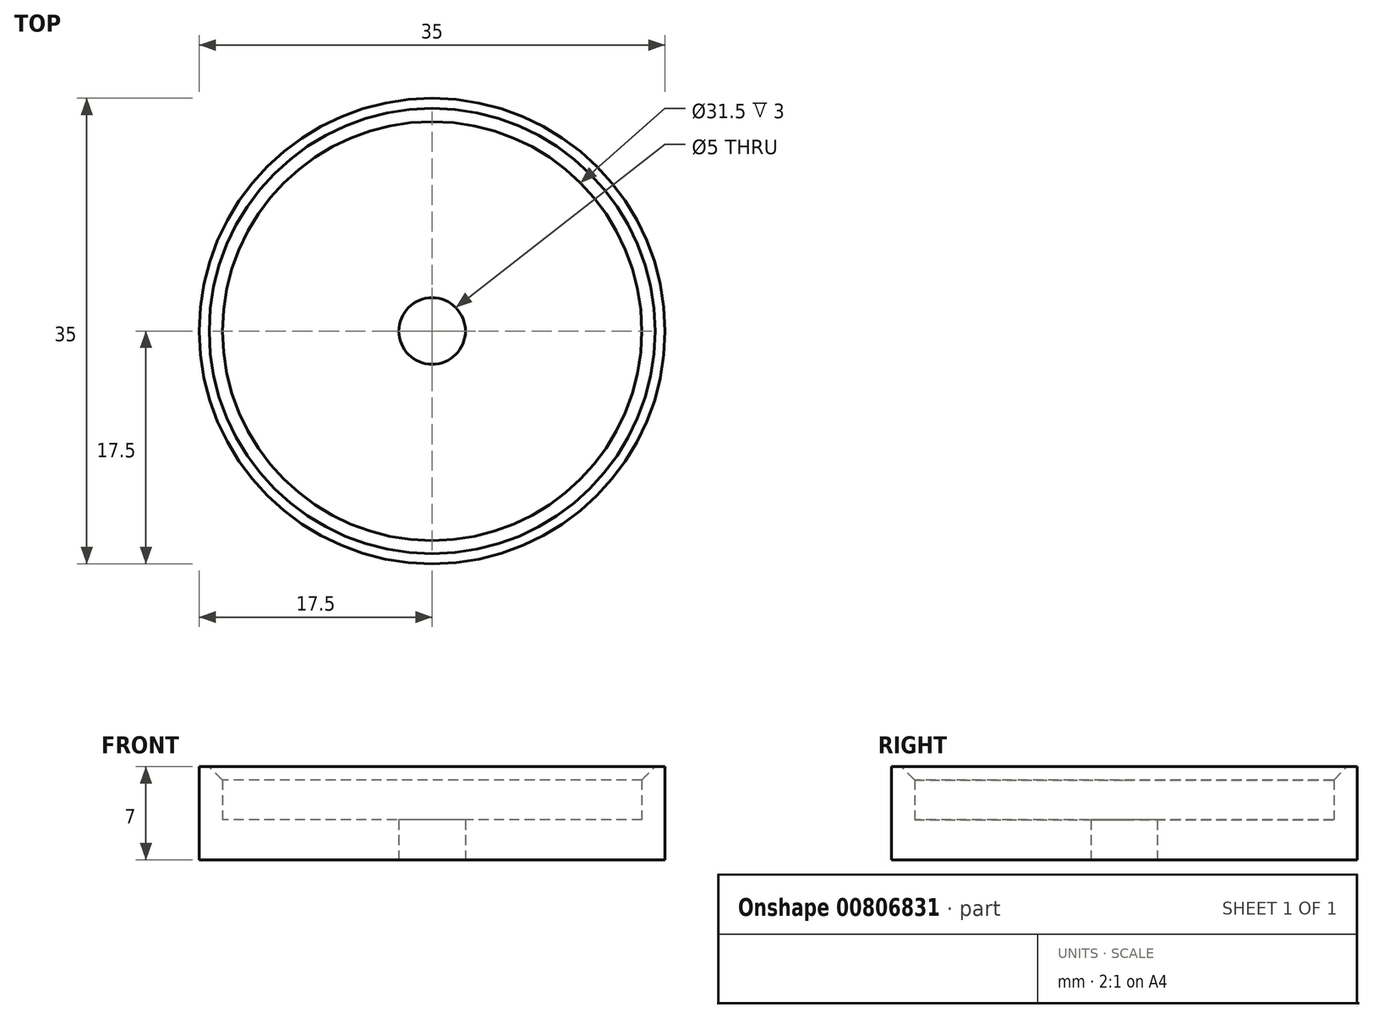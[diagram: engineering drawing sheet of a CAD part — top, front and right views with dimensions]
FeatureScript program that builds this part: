
annotation { "Feature Type Name" : "Feature", "Feature Type Description" : "" }
export const myFeature = defineFeature(function(context is Context, id is Id, definition is map)
    precondition{}
    {
        {
            var Q0;
            Q0=qCreatedBy(makeId("Top.planeOp"),FACE);
            var sketch = newSketch(context, id + "F0", { "sketchPlane" : qUnion([Q0])});
            skCircle(sketch, "E0", {"center": v(0, 0) * mm, "radius": 17.5 * mm});
            skCircle(sketch, "E1", {"center": v(0, 0) * mm, "radius": 15.75 * mm});
            skCircle(sketch, "E2", {"center": v(0, 0) * mm, "radius": 2.5 * mm});
            skSolve(sketch);
        }
        {
            var Q0;
            Q0=makeQuery(id+"F0.imprint","IMPRINT",FACE,{"disambiguationData":[TD([[makeQuery(id+"F0.imprint","IMPRINT",EDGE,{"derivedFrom":sQuery(id+"F0.wireOp",EDGE,"E0")}),1.0]])]});
            var Q1;
            {var subQ0=sQuery(id+"F0.wireOp",EDGE,"xPpbhzml-UGrW-7zZY-eOFT-DjyW9iULf8BB.bottom");var subQ1=sQuery(id+"F0.wireOp",EDGE,"E0");var subQ2=makeQuery(id+"F0.imprint","INTERSECT",VERTEX,{"disambiguationData":[OD(1.0)],"derivedFrom":[subQ1,subQ0]});Q1=makeQuery(id+"F0.imprint","IMPRINT",FACE,{"disambiguationData":[TD([[makeQuery(id+"F0.imprint","IMPRINT",EDGE,{"disambiguationData":[TD([[subQ2,-1.0]])],"derivedFrom":subQ1}),1.0]])]});}
            var Q2;
            {var subQ0=sQuery(id+"F0.wireOp",EDGE,"hrvuodh3-IVyE-woEC-Gxd3-sxO2CLI6YTkv.right");var subQ1=sQuery(id+"F0.wireOp",EDGE,"E0");var subQ2=makeQuery(id+"F0.imprint","INTERSECT",VERTEX,{"disambiguationData":[OD(1.0)],"derivedFrom":[subQ1,subQ0]});Q2=makeQuery(id+"F0.imprint","IMPRINT",FACE,{"disambiguationData":[TD([[makeQuery(id+"F0.imprint","IMPRINT",EDGE,{"disambiguationData":[TD([[subQ2,-1.0]])],"derivedFrom":subQ1}),1.0]])]});}
            var Q3;
            {var subQ0=sQuery(id+"F0.wireOp",EDGE,"xPpbhzml-UGrW-7zZY-eOFT-DjyW9iULf8BB.bottom");var subQ1=sQuery(id+"F0.wireOp",EDGE,"E0");var subQ2=makeQuery(id+"F0.imprint","INTERSECT",VERTEX,{"disambiguationData":[OD(0.0)],"derivedFrom":[subQ1,subQ0]});Q3=makeQuery(id+"F0.imprint","IMPRINT",FACE,{"disambiguationData":[TD([[makeQuery(id+"F0.imprint","IMPRINT",EDGE,{"disambiguationData":[TD([[subQ2,1.0]])],"derivedFrom":subQ1}),1.0]])]});}
            var Q4;
            {var subQ0=sQuery(id+"F0.wireOp",EDGE,"hrvuodh3-IVyE-woEC-Gxd3-sxO2CLI6YTkv.left");var subQ1=sQuery(id+"F0.wireOp",EDGE,"E0");var subQ2=makeQuery(id+"F0.imprint","INTERSECT",VERTEX,{"disambiguationData":[OD(0.0)],"derivedFrom":[subQ1,subQ0]});Q4=makeQuery(id+"F0.imprint","IMPRINT",FACE,{"disambiguationData":[TD([[makeQuery(id+"F0.imprint","IMPRINT",EDGE,{"disambiguationData":[TD([[subQ2,-1.0]])],"derivedFrom":subQ1}),1.0]])]});}
            var Q5;
            Q5=makeQuery(id+"F0.imprint","IMPRINT",FACE,{"disambiguationData":[TD([[makeQuery(id+"F0.imprint","IMPRINT",EDGE,{"derivedFrom":sQuery(id+"F0.wireOp",EDGE,"E1")}),-1.0]])]});
            extrude(context, id + "F1", {"entities" : qUnion([Q0, Q1, Q2, Q3, Q4, Q5]), "depth" : 7 * mm, "offsetDistance" : 25 * mm});
        }
        {
            var Q0;
            Q0=makeQuery(id+"F0.imprint","IMPRINT",FACE,{"disambiguationData":[TD([[makeQuery(id+"F0.imprint","IMPRINT",EDGE,{"derivedFrom":sQuery(id+"F0.wireOp",EDGE,"E2")}),-1.0]])]});
            var Q1;
            {var subQ0=sQuery(id+"F0.wireOp",EDGE,"xPpbhzml-UGrW-7zZY-eOFT-DjyW9iULf8BB.bottom");var subQ1=sQuery(id+"F0.wireOp",EDGE,"E1");var subQ2=makeQuery(id+"F0.imprint","INTERSECT",VERTEX,{"disambiguationData":[OD(0.0)],"derivedFrom":[subQ1,subQ0]});Q1=makeQuery(id+"F0.imprint","IMPRINT",FACE,{"disambiguationData":[TD([[makeQuery(id+"F0.imprint","IMPRINT",EDGE,{"disambiguationData":[TD([[subQ2,-1.0]])],"derivedFrom":subQ1}),1.0]])]});}
            var Q2;
            {var subQ0=sQuery(id+"F0.wireOp",EDGE,"hrvuodh3-IVyE-woEC-Gxd3-sxO2CLI6YTkv.right");var subQ1=sQuery(id+"F0.wireOp",EDGE,"E1");var subQ2=makeQuery(id+"F0.imprint","INTERSECT",VERTEX,{"disambiguationData":[OD(0.0)],"derivedFrom":[subQ1,subQ0]});Q2=makeQuery(id+"F0.imprint","IMPRINT",FACE,{"disambiguationData":[TD([[makeQuery(id+"F0.imprint","IMPRINT",EDGE,{"disambiguationData":[TD([[subQ2,-1.0]])],"derivedFrom":subQ1}),1.0]])]});}
            var Q3;
            {var subQ0=sQuery(id+"F0.wireOp",EDGE,"xPpbhzml-UGrW-7zZY-eOFT-DjyW9iULf8BB.top");var subQ1=sQuery(id+"F0.wireOp",EDGE,"E1");var subQ2=makeQuery(id+"F0.imprint","INTERSECT",VERTEX,{"disambiguationData":[OD(0.0)],"derivedFrom":[subQ1,subQ0]});Q3=makeQuery(id+"F0.imprint","IMPRINT",FACE,{"disambiguationData":[TD([[makeQuery(id+"F0.imprint","IMPRINT",EDGE,{"disambiguationData":[TD([[subQ2,-1.0]])],"derivedFrom":subQ1}),1.0]])]});}
            var Q4;
            {var subQ0=sQuery(id+"F0.wireOp",EDGE,"hrvuodh3-IVyE-woEC-Gxd3-sxO2CLI6YTkv.left");var subQ1=sQuery(id+"F0.wireOp",EDGE,"E1");var subQ2=makeQuery(id+"F0.imprint","INTERSECT",VERTEX,{"disambiguationData":[OD(0.0)],"derivedFrom":[subQ1,subQ0]});Q4=makeQuery(id+"F0.imprint","IMPRINT",FACE,{"disambiguationData":[TD([[makeQuery(id+"F0.imprint","IMPRINT",EDGE,{"disambiguationData":[TD([[subQ2,1.0]])],"derivedFrom":subQ1}),1.0]])]});}
            extrude(context, id + "F2", {"entities" : qUnion([Q0, Q1, Q2, Q3, Q4]), "operationType" : NewBodyOperationType.ADD, "depth" : 3 * mm, "offsetDistance" : 25 * mm});
        }
        {
            var Q0;
            Q0=makeQuery(id+"F1.opExtrude","CAP_EDGE",EDGE,{"disambiguationData":[OSD([sQuery(id+"F0.wireOp",EDGE,"E1")])],"isStart":false});
            chamfer(context, id + "F3", {"entities" : qUnion([Q0]), "width" : 1 * mm, "tangentPropagation" : true});
        }
    });
